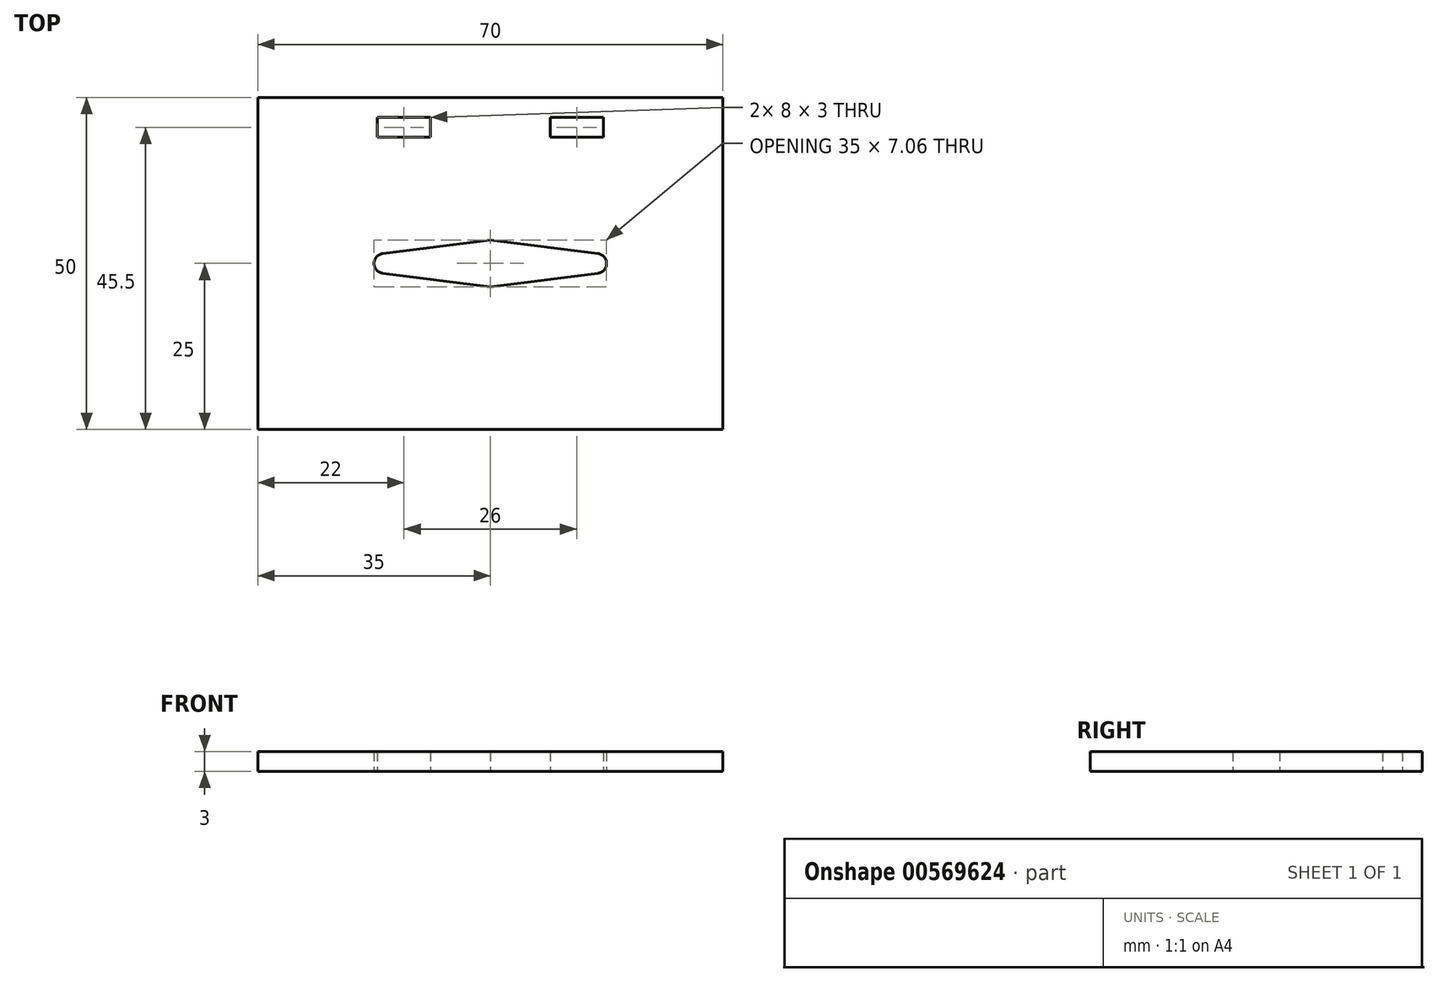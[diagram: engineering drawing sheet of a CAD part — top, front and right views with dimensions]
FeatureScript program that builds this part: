
annotation { "Feature Type Name" : "Feature", "Feature Type Description" : "" }
export const myFeature = defineFeature(function(context is Context, id is Id, definition is map)
    precondition{}
    {
        {
            var Q0;
            Q0=qCreatedBy(makeId("Top.planeOp"),FACE);
            var sketch = newSketch(context, id + "F0", { "sketchPlane" : qUnion([Q0])});
            skLineSegment(sketch, "E0.bottom", {"start": v(-35, 25) * mm, "end": v(35, 25) * mm});
            skLineSegment(sketch, "E0.top", {"start": v(-35, -25) * mm, "end": v(35, -25) * mm});
            skLineSegment(sketch, "E0.left", {"start": v(-35, 25) * mm, "end": v(-35, -25) * mm});
            skLineSegment(sketch, "E0.right", {"start": v(35, 25) * mm, "end": v(35, -25) * mm});
            skLineSegment(sketch, "E1", {"start": v(-46.2, 19) * mm, "end": v(68.04, 19) * mm, "construction": true});
            skLineSegment(sketch, "E2", {"start": v(-46.48, 22) * mm, "end": v(68.04, 22) * mm, "construction": true});
            skLineSegment(sketch, "E3.bottom", {"start": v(-17, 22) * mm, "end": v(-9, 22) * mm});
            skLineSegment(sketch, "E3.top", {"start": v(-17, 19) * mm, "end": v(-9, 19) * mm});
            skLineSegment(sketch, "E3.left", {"start": v(-17, 22) * mm, "end": v(-17, 19) * mm});
            skLineSegment(sketch, "E3.right", {"start": v(-9, 22) * mm, "end": v(-9, 19) * mm});
            skLineSegment(sketch, "E4.bottom", {"start": v(9, 22) * mm, "end": v(17, 22) * mm});
            skLineSegment(sketch, "E4.top", {"start": v(9, 19) * mm, "end": v(17, 19) * mm});
            skLineSegment(sketch, "E4.left", {"start": v(9, 22) * mm, "end": v(9, 19) * mm});
            skLineSegment(sketch, "E4.right", {"start": v(17, 22) * mm, "end": v(17, 19) * mm});
            skArc(sketch, "E5", {"start": v(0.44, 3.47) * mm, "mid": v(0, 3.5) * mm, "end": v(-0.44, 3.47) * mm});
            skArc(sketch, "E6", {"start": v(-16.19, 1.49) * mm, "mid": v(-17.5, 0) * mm, "end": v(-16.19, -1.49) * mm});
            skArc(sketch, "E7", {"start": v(16.19, -1.49) * mm, "mid": v(17.5, 0) * mm, "end": v(16.19, 1.49) * mm});
            skLineSegment(sketch, "E8", {"start": v(-16.19, 1.49) * mm, "end": v(0, 3.53) * mm});
            skLineSegment(sketch, "E9", {"start": v(0, 3.53) * mm, "end": v(16.19, 1.49) * mm});
            skLineSegment(sketch, "E10", {"start": v(16.19, -1.49) * mm, "end": v(0, -3.53) * mm});
            skLineSegment(sketch, "E11", {"start": v(0, -3.53) * mm, "end": v(-16.19, -1.49) * mm});
            skArc(sketch, "E12.trimOffspring", {"start": v(-0.44, -3.47) * mm, "mid": v(0, -3.5) * mm, "end": v(0.44, -3.47) * mm});
            skSolve(sketch);
        }
        {
            var Q0;
            Q0=makeQuery(id+"F0.imprint","IMPRINT",FACE,{"disambiguationData":[TD([[makeQuery(id+"F0.imprint","IMPRINT",EDGE,{"derivedFrom":sQuery(id+"F0.wireOp",EDGE,"E0.bottom")}),-1.0]])]});
            extrude(context, id + "F1", {"entities" : qUnion([Q0]), "depth" : 3 * mm, "offsetDistance" : 25 * mm});
        }
    });
